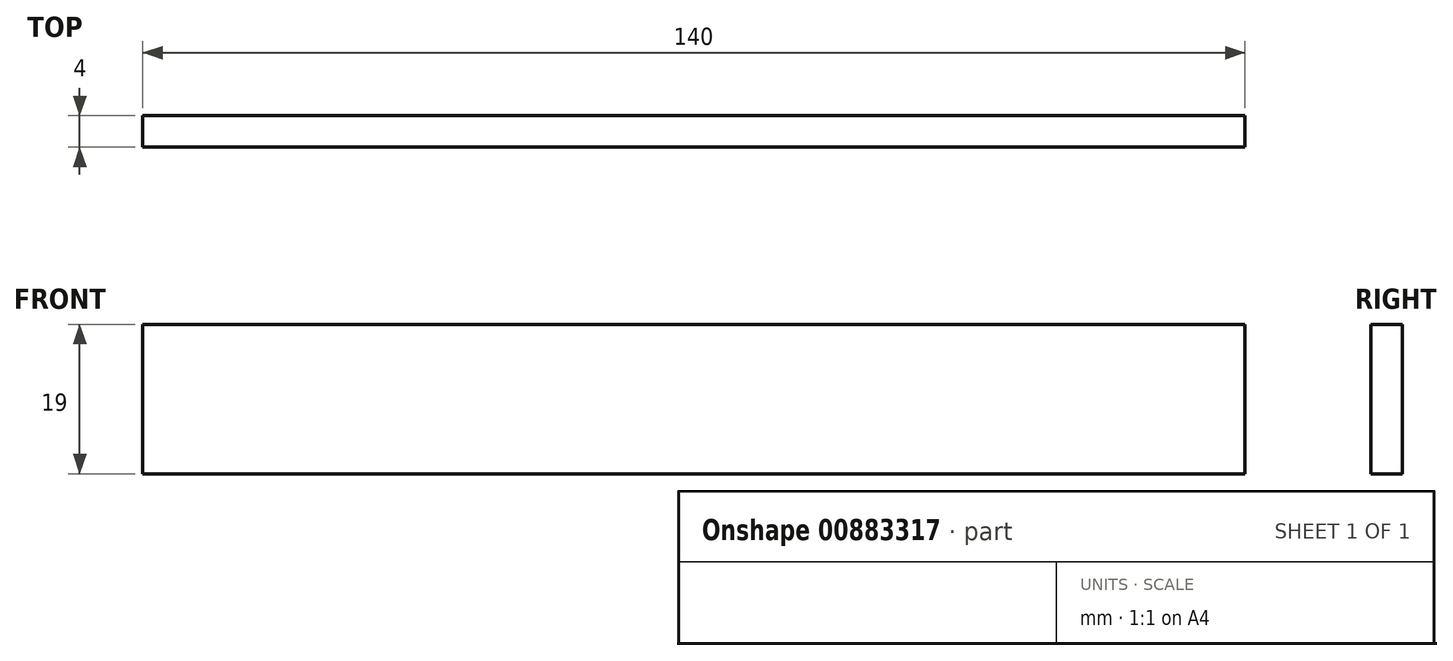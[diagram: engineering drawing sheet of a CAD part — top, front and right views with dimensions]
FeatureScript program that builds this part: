
annotation { "Feature Type Name" : "Feature", "Feature Type Description" : "" }
export const myFeature = defineFeature(function(context is Context, id is Id, definition is map)
    precondition{}
    {
        {
            var Q0;
            Q0=qCreatedBy(makeId("Front.planeOp"),FACE);
            var sketch = newSketch(context, id + "F0", { "sketchPlane" : qUnion([Q0])});
            skLineSegment(sketch, "E0.bottom", {"start": v(1.89, 9.04) * mm, "end": v(141.89, 9.04) * mm});
            skLineSegment(sketch, "E0.top", {"start": v(1.89, -9.96) * mm, "end": v(141.89, -9.96) * mm});
            skLineSegment(sketch, "E0.left", {"start": v(1.89, 9.04) * mm, "end": v(1.89, -9.96) * mm});
            skLineSegment(sketch, "E0.right", {"start": v(141.89, 9.04) * mm, "end": v(141.89, -9.96) * mm});
            skSolve(sketch);
        }
        {
            var Q0;
            Q0=makeQuery(id+"F0.imprint","IMPRINT",FACE,{"disambiguationData":[TD([[makeQuery(id+"F0.imprint","IMPRINT",EDGE,{"derivedFrom":sQuery(id+"F0.wireOp",EDGE,"E0.bottom")}),-1.0]])]});
            extrude(context, id + "F1", {"entities" : qUnion([Q0]), "depth" : 4 * mm, "offsetDistance" : 25 * mm});
        }
    });
